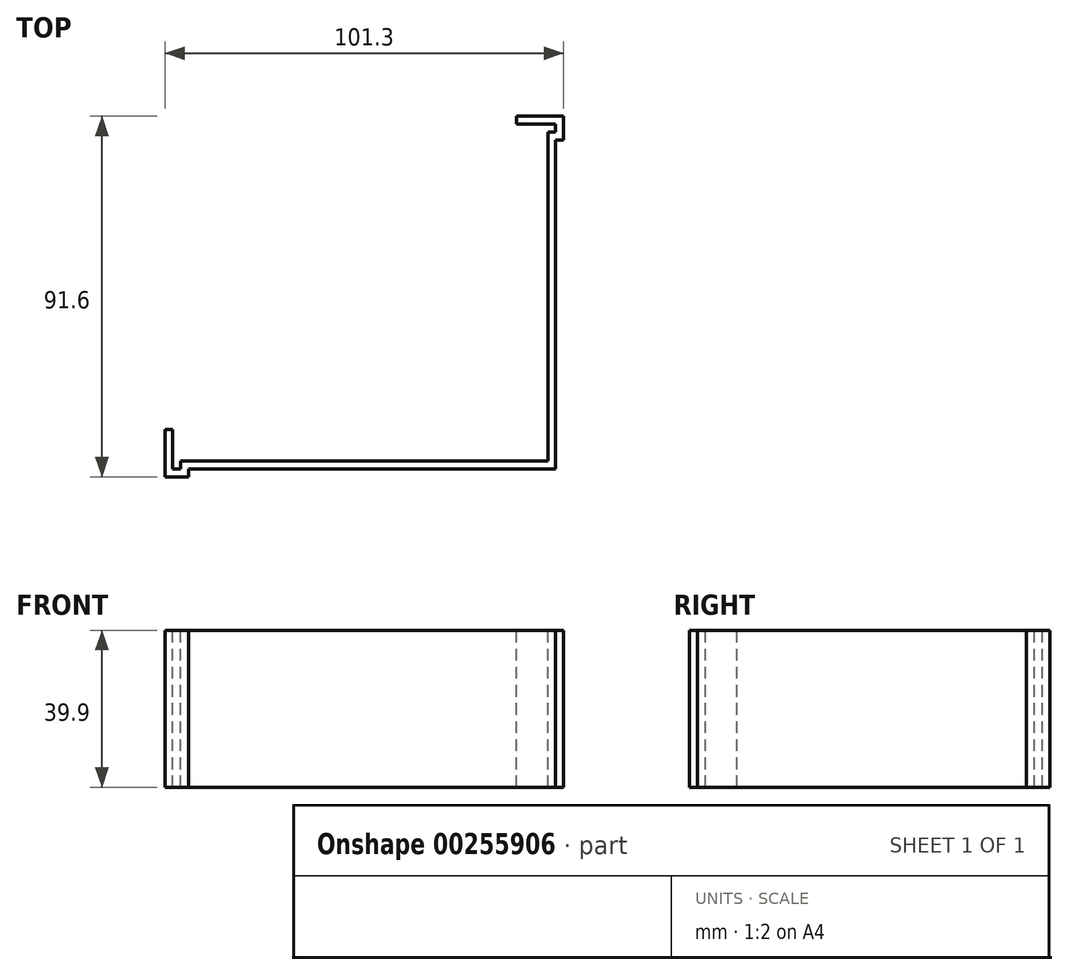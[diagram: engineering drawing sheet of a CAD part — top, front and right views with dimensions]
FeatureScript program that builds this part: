
annotation { "Feature Type Name" : "Feature", "Feature Type Description" : "" }
export const myFeature = defineFeature(function(context is Context, id is Id, definition is map)
    precondition{}
    {
        {
            var Q0;
            Q0=qCreatedBy(makeId("Top.planeOp"),FACE);
            var sketch = newSketch(context, id + "F0", { "sketchPlane" : qUnion([Q0])});
            skLineSegment(sketch, "E0.bottom", {"start": v(50.65, -45.8) * mm, "end": v(-50.65, -45.8) * mm});
            skLineSegment(sketch, "E0.top", {"start": v(50.65, 45.8) * mm, "end": v(-50.65, 45.8) * mm});
            skLineSegment(sketch, "E0.left", {"start": v(50.65, -45.8) * mm, "end": v(50.65, 45.8) * mm});
            skLineSegment(sketch, "E0.right", {"start": v(-50.65, -45.8) * mm, "end": v(-50.65, 45.8) * mm});
            skPoint(sketch, "E0.middle", {"position": v(0, 0) * mm});
            skSolve(sketch);
        }
        {
            var Q0;
            Q0 = qSketchRegion(id + "F0", true);
            extrude(context, id + "F1", {"entities" : qUnion([Q0]), "depth" : 39.9 * mm});
        }
        {
            var Q0;
            Q0=makeQuery(id+"F1.opExtrude","CAP_FACE",FACE,{"disambiguationData":[OSD([sQuery(id+"F0.wireOp",EDGE,"E0.bottom"),sQuery(id+"F0.wireOp",EDGE,"E0.top"),sQuery(id+"F0.wireOp",EDGE,"E0.left"),sQuery(id+"F0.wireOp",EDGE,"E0.right")])],"isStart":false});
            var sketch = newSketch(context, id + "F2", { "sketchPlane" : qUnion([Q0])});
            skLineSegment(sketch, "E1", {"start": v(-50.65, 45.8) * mm, "end": v(-50.65, -33.8) * mm});
            skLineSegment(sketch, "E2", {"start": v(-50.65, -33.8) * mm, "end": v(-48.65, -33.8) * mm});
            skLineSegment(sketch, "E3", {"start": v(-48.65, -33.8) * mm, "end": v(-48.65, -43.8) * mm});
            skLineSegment(sketch, "E4", {"start": v(46.65, -41.8) * mm, "end": v(46.65, 41.8) * mm});
            skLineSegment(sketch, "E5", {"start": v(48.65, 43.8) * mm, "end": v(38.65, 43.8) * mm});
            skLineSegment(sketch, "E6", {"start": v(38.65, 43.8) * mm, "end": v(38.65, 45.8) * mm});
            skLineSegment(sketch, "E7", {"start": v(38.65, 45.8) * mm, "end": v(-50.65, 45.8) * mm});
            skLineSegment(sketch, "E8", {"start": v(46.65, 41.8) * mm, "end": v(48.65, 41.8) * mm});
            skLineSegment(sketch, "E9", {"start": v(48.65, 41.8) * mm, "end": v(48.65, 43.8) * mm});
            skLineSegment(sketch, "E10", {"start": v(-46.65, -41.8) * mm, "end": v(46.65, -41.8) * mm});
            skLineSegment(sketch, "E11", {"start": v(-48.65, -43.8) * mm, "end": v(-46.65, -43.8) * mm});
            skLineSegment(sketch, "E12", {"start": v(-46.65, -43.8) * mm, "end": v(-46.65, -41.8) * mm});
            skSolve(sketch);
        }
        {
            var Q0;
            Q0 = qSketchRegion(id + "F2", true);
            extrude(context, id + "F3", {"entities" : qUnion([Q0]), "operationType" : NewBodyOperationType.REMOVE, "oppositeDirection" : true, "depth" : 44.9 * mm});
        }
        {
            var Q0;
            Q0=makeQuery(id+"F1.opExtrude","CAP_FACE",FACE,{"disambiguationData":[OSD([sQuery(id+"F0.wireOp",EDGE,"E0.bottom"),sQuery(id+"F0.wireOp",EDGE,"E0.top"),sQuery(id+"F0.wireOp",EDGE,"E0.left"),sQuery(id+"F0.wireOp",EDGE,"E0.right")])],"isStart":true});
            var sketch = newSketch(context, id + "F4", { "sketchPlane" : qUnion([Q0])});
            skLineSegment(sketch, "E13.bottom", {"start": v(45.65, -40.8) * mm, "end": v(-45.65, -40.8) * mm});
            skLineSegment(sketch, "E13.top", {"start": v(45.65, 40.8) * mm, "end": v(-45.65, 40.8) * mm});
            skLineSegment(sketch, "E13.left", {"start": v(45.65, -40.8) * mm, "end": v(45.65, 40.8) * mm});
            skLineSegment(sketch, "E13.right", {"start": v(-45.65, -40.8) * mm, "end": v(-45.65, 40.8) * mm});
            skPoint(sketch, "E13.middle", {"position": v(0, 0) * mm});
            skSolve(sketch);
        }
        {
            var Q0;
            Q0 = qSketchRegion(id + "F4", true);
            extrude(context, id + "F5", {"entities" : qUnion([Q0]), "operationType" : NewBodyOperationType.REMOVE, "oppositeDirection" : true, "depth" : 25 * mm});
        }
        {
            var Q0;
            Q0=makeQuery(id+"F1.opExtrude","CAP_FACE",FACE,{"disambiguationData":[OSD([sQuery(id+"F0.wireOp",EDGE,"E0.bottom"),sQuery(id+"F0.wireOp",EDGE,"E0.top"),sQuery(id+"F0.wireOp",EDGE,"E0.left"),sQuery(id+"F0.wireOp",EDGE,"E0.right")])],"isStart":false});
            var sketch = newSketch(context, id + "F6", { "sketchPlane" : qUnion([Q0])});
            skLineSegment(sketch, "E14", {"start": v(50.65, -45.8) * mm, "end": v(50.65, 39.8) * mm});
            skLineSegment(sketch, "E15", {"start": v(50.65, 39.8) * mm, "end": v(48.65, 39.8) * mm});
            skLineSegment(sketch, "E16", {"start": v(48.65, 39.8) * mm, "end": v(48.65, -43.8) * mm});
            skLineSegment(sketch, "E17", {"start": v(48.65, -43.8) * mm, "end": v(-44.65, -43.8) * mm});
            skLineSegment(sketch, "E18", {"start": v(-44.65, -43.8) * mm, "end": v(-44.65, -45.8) * mm});
            skLineSegment(sketch, "E19", {"start": v(-44.65, -45.8) * mm, "end": v(50.65, -45.8) * mm});
            skSolve(sketch);
        }
        {
            var Q0;
            Q0 = qSketchRegion(id + "F6", true);
            extrude(context, id + "F7", {"entities" : qUnion([Q0]), "operationType" : NewBodyOperationType.REMOVE, "oppositeDirection" : true, "depth" : 40 * mm});
        }
    });
